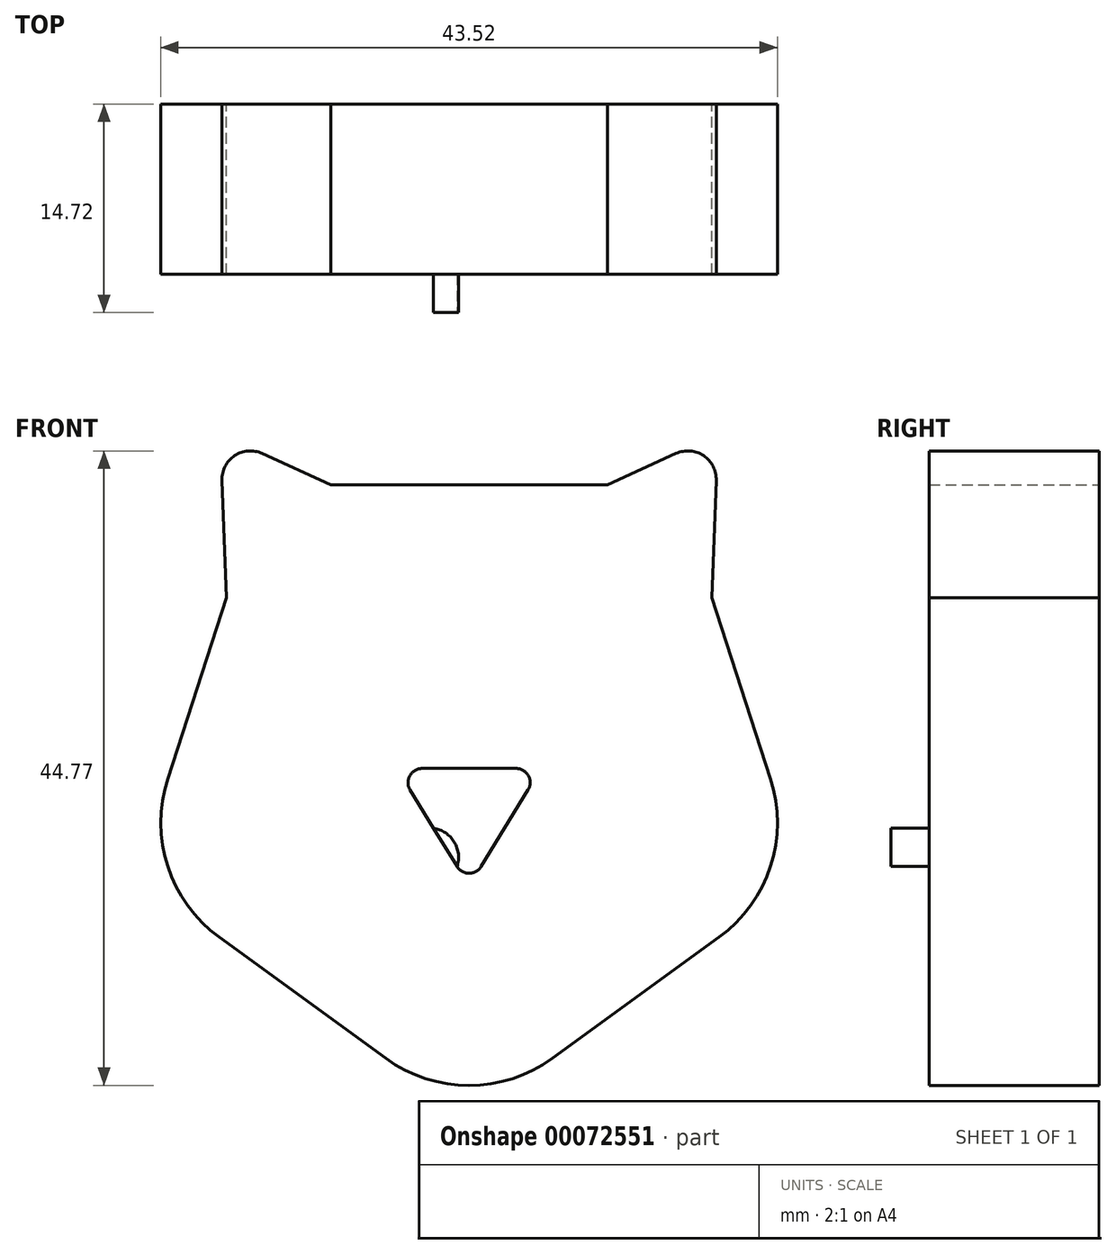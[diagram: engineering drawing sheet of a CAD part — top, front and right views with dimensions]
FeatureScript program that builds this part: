
annotation { "Feature Type Name" : "Feature", "Feature Type Description" : "" }
export const myFeature = defineFeature(function(context is Context, id is Id, definition is map)
    precondition{}
    {
        {
            var Q0;
            Q0=qCreatedBy(makeId("Front.planeOp"),FACE);
            var sketch = newSketch(context, id + "F0", { "sketchPlane" : qUnion([Q0])});
            skCircle(sketch, "E0.cCircle", {"center": v(0, 0) * mm, "radius": 20 * mm, "construction": true});
            skLineSegment(sketch, "E0.0", {"start": v(0, -24.72) * mm, "end": v(-23.51, -7.64) * mm});
            skLineSegment(sketch, "E0.1", {"start": v(-23.51, -7.64) * mm, "end": v(-14.53, 20) * mm});
            skLineSegment(sketch, "E0.2", {"start": v(-14.53, 20) * mm, "end": v(14.53, 20) * mm});
            skLineSegment(sketch, "E0.3", {"start": v(14.53, 20) * mm, "end": v(23.51, -7.64) * mm});
            skLineSegment(sketch, "E0.4", {"start": v(23.51, -7.64) * mm, "end": v(0, -24.72) * mm});
            skPoint(sketch, "E0.0.midPoint", {"position": v(-11.76, -16.18) * mm});
            skPoint(sketch, "E1.0.midPoint", {"position": v(19.33, 5.13) * mm});
            skSolve(sketch);
        }
        {
            var Q0;
            Q0=makeQuery(id+"F0.imprint","IMPRINT",FACE,{"disambiguationData":[TD([[makeQuery(id+"F0.imprint","IMPRINT",EDGE,{"derivedFrom":sQuery(id+"F0.wireOp",EDGE,"E0.0")}),-1.0]])]});
            extrude(context, id + "F1", {"entities" : qUnion([Q0]), "endBound" : BoundingType.SYMMETRIC, "depth" : 12 * mm});
        }
        {
            var Q0;
            Q0=qCreatedBy(makeId("Front.planeOp"),FACE);
            var sketch = newSketch(context, id + "F2", { "sketchPlane" : qUnion([Q0])});
            skLineSegment(sketch, "E2", {"start": v(-17.12, 12.04) * mm, "end": v(-17.56, 23.58) * mm});
            skLineSegment(sketch, "E3", {"start": v(-17.56, 23.58) * mm, "end": v(-9.75, 20) * mm});
            skLineSegment(sketch, "E4", {"start": v(-9.75, 20) * mm, "end": v(-17.12, 12.04) * mm});
            skLineSegment(sketch, "E5", {"start": v(0, 29) * mm, "end": v(0, 12.45) * mm});
            skLineSegment(sketch, "E6.MirrorCS", {"start": v(9.75, 20) * mm, "end": v(17.12, 12.04) * mm});
            skLineSegment(sketch, "E7.MirrorCS", {"start": v(17.56, 23.58) * mm, "end": v(9.75, 20) * mm});
            skLineSegment(sketch, "E8.MirrorCS", {"start": v(17.12, 12.04) * mm, "end": v(17.56, 23.58) * mm});
            skSolve(sketch);
        }
        {
            var Q0;
            Q0=makeQuery(id+"F2.imprint","IMPRINT",FACE,{"disambiguationData":[TD([[makeQuery(id+"F2.imprint","IMPRINT",EDGE,{"derivedFrom":sQuery(id+"F2.wireOp",EDGE,"E2")}),-1.0]])]});
            var Q1;
            Q1=makeQuery(id+"F2.imprint","IMPRINT",FACE,{"disambiguationData":[TD([[makeQuery(id+"F2.imprint","IMPRINT",EDGE,{"derivedFrom":sQuery(id+"F2.wireOp",EDGE,"E6.MirrorCS")}),1.0]])]});
            extrude(context, id + "F3", {"entities" : qUnion([Q0, Q1]), "operationType" : NewBodyOperationType.ADD, "endBound" : BoundingType.SYMMETRIC, "depth" : 12 * mm});
        }
        {
            var Q0;
            Q0=qCreatedBy(makeId("Front.planeOp"),FACE);
            var sketch = newSketch(context, id + "F4", { "sketchPlane" : qUnion([Q0])});
            skLineSegment(sketch, "E9", {"start": v(-21.03, 0) * mm, "end": v(0, 0) * mm, "construction": true});
            skLineSegment(sketch, "E10", {"start": v(-10.51, 0) * mm, "end": v(-10.51, 5.14) * mm, "construction": true});
            skCircle(sketch, "E11", {"center": v(-10.51, 5.14) * mm, "radius": 3.67 * mm});
            skLineSegment(sketch, "E12", {"start": v(0, 0) * mm, "end": v(0, 12.57) * mm, "construction": true});
            skCircle(sketch, "E13.MirrorC", {"center": v(10.51, 5.14) * mm, "radius": 3.67 * mm});
            skSolve(sketch);
        }
        {
            var Q0;
            Q0=makeQuery(id+"F3.opExtrude","SWEPT_EDGE",EDGE,{"disambiguationData":[OSD([sQuery(id+"F2.wireOp",EDGE,"E2"),sQuery(id+"F2.wireOp",EDGE,"E3")])]});
            var Q1;
            Q1=makeQuery(id+"F3.opExtrude","SWEPT_EDGE",EDGE,{"disambiguationData":[OSD([sQuery(id+"F2.wireOp",EDGE,"E7.MirrorCS"),sQuery(id+"F2.wireOp",EDGE,"E8.MirrorCS")])]});
            fillet(context, id + "F5", {"entities" : qUnion([Q0, Q1]), "radius" : 2 * mm, "tangentPropagation" : true, "allowEdgeOverflow" : false});
        }
        {
            var Q0;
            Q0=makeQuery(id+"F1.opExtrude","SWEPT_EDGE",EDGE,{"disambiguationData":[OSD([sQuery(id+"F0.wireOp",EDGE,"E0.0"),sQuery(id+"F0.wireOp",EDGE,"E0.1")])]});
            var Q1;
            Q1=makeQuery(id+"F1.opExtrude","SWEPT_EDGE",EDGE,{"disambiguationData":[OSD([sQuery(id+"F0.wireOp",EDGE,"E0.3"),sQuery(id+"F0.wireOp",EDGE,"E0.4")])]});
            var Q2;
            Q2=makeQuery(id+"F1.opExtrude","SWEPT_EDGE",EDGE,{"disambiguationData":[OSD([sQuery(id+"F0.wireOp",EDGE,"E0.0"),sQuery(id+"F0.wireOp",EDGE,"E0.4")])]});
            fillet(context, id + "F6", {"entities" : qUnion([Q0, Q1, Q2]), "radius" : 10 * mm, "tangentPropagation" : true, "allowEdgeOverflow" : false});
        }
        {
            var Q0;
            Q0=sQuery(id+"F4.wireOp",EDGE,"E11");
            var Q1;
            Q1=sQuery(id+"F4.wireOp",EDGE,"E13.MirrorC");
            extrude(context, id + "F7", {"bodyType" : ToolBodyType.SURFACE, "surfaceEntities" : qUnion([Q0, Q1]), "depth" : 7 * mm});
        }
        {
            var Q0;
            Q0=makeQuery(id+"F3.boolean.opBoolean","MERGE",FACE,{"derivedFrom":[makeQuery(id+"F1.opExtrude","CAP_FACE",FACE,{"disambiguationData":[OSD([sQuery(id+"F0.wireOp",EDGE,"E0.0"),sQuery(id+"F0.wireOp",EDGE,"E0.1"),sQuery(id+"F0.wireOp",EDGE,"E0.2"),sQuery(id+"F0.wireOp",EDGE,"E0.3"),sQuery(id+"F0.wireOp",EDGE,"E0.4")])],"isStart":false}),makeQuery(id+"F3.opExtrude","CAP_FACE",FACE,{"disambiguationData":[OSD([sQuery(id+"F2.wireOp",EDGE,"E2"),sQuery(id+"F2.wireOp",EDGE,"E3"),sQuery(id+"F2.wireOp",EDGE,"E4")])],"isStart":false}),makeQuery(id+"F3.opExtrude","CAP_FACE",FACE,{"disambiguationData":[OSD([sQuery(id+"F2.wireOp",EDGE,"E6.MirrorCS"),sQuery(id+"F2.wireOp",EDGE,"E7.MirrorCS"),sQuery(id+"F2.wireOp",EDGE,"E8.MirrorCS")])],"isStart":false})]});
            var sketch = newSketch(context, id + "F8", { "sketchPlane" : qUnion([Q0])});
            skLineSegment(sketch, "E14", {"start": v(-5.1, 0) * mm, "end": v(5.1, 0) * mm});
            skLineSegment(sketch, "E15", {"start": v(5.1, 0) * mm, "end": v(0, -8.32) * mm});
            skLineSegment(sketch, "E16", {"start": v(0, -8.32) * mm, "end": v(-5.1, 0) * mm});
            skSolve(sketch);
        }
        {
            var Q0;
            Q0=makeQuery(id+"F8.imprint","IMPRINT",FACE,{"disambiguationData":[TD([[makeQuery(id+"F8.imprint","IMPRINT",EDGE,{"derivedFrom":sQuery(id+"F8.wireOp",EDGE,"E14")}),-1.0]])]});
            extrude(context, id + "F9", {"entities" : qUnion([Q0]), "operationType" : NewBodyOperationType.ADD, "depth" : 2.72 * mm});
        }
        {
            var Q0;
            Q0=makeQuery(id+"F9.opExtrude","SWEPT_EDGE",EDGE,{"disambiguationData":[OSD([sQuery(id+"F8.wireOp",EDGE,"E15"),sQuery(id+"F8.wireOp",EDGE,"E16")])]});
            var Q1;
            Q1=makeQuery(id+"F9.opExtrude","SWEPT_EDGE",EDGE,{"disambiguationData":[OSD([sQuery(id+"F8.wireOp",EDGE,"E14"),sQuery(id+"F8.wireOp",EDGE,"E16")])]});
            var Q2;
            Q2=makeQuery(id+"F9.opExtrude","SWEPT_EDGE",EDGE,{"disambiguationData":[OSD([sQuery(id+"F8.wireOp",EDGE,"E14"),sQuery(id+"F8.wireOp",EDGE,"E15")])]});
            fillet(context, id + "F10", {"entities" : qUnion([Q0, Q1, Q2]), "radius" : 1 * mm, "tangentPropagation" : true, "allowEdgeOverflow" : false});
        }
        {
            var Q0;
            Q0=qCreatedBy(makeId("Front.planeOp"),FACE);
            cPlane(context, id + "F11", {"entities" : qUnion([Q0]), "cplaneType" : CPlaneType.OFFSET, "offset" : 8 * mm, "width" : 152.4 * mm, "height" : 152.4 * mm});
        }
        {
            var Q0;
            Q0=qCreatedBy(id+"F11.planeOp",FACE);
            var sketch = newSketch(context, id + "F12", { "sketchPlane" : qUnion([Q0])});
            skLineSegment(sketch, "E17", {"start": v(-10.51, 8.81) * mm, "end": v(-10.51, 1.48) * mm, "construction": true});
            skLineSegment(sketch, "E18", {"start": v(0, 8.43) * mm, "end": v(0, 3.77) * mm, "construction": true});
            skLineSegment(sketch, "E19.MirrorCS", {"start": v(10.51, 8.81) * mm, "end": v(10.51, 1.48) * mm, "construction": true});
            skPoint(sketch, "E20", {"position": v(-10.51, 5.14) * mm});
            skPoint(sketch, "E21", {"position": v(10.51, 5.14) * mm});
            skSolve(sketch);
        }
        {
            var Q0;
            Q0=sQuery(id+"F12.wireOp",VERTEX,"E20");
            var Q1;
            Q1=makeQuery(id+"F3.boolean.opBoolean","MERGE",FACE,{"derivedFrom":[makeQuery(id+"F1.opExtrude","CAP_FACE",FACE,{"disambiguationData":[OSD([sQuery(id+"F0.wireOp",EDGE,"E0.0"),sQuery(id+"F0.wireOp",EDGE,"E0.1"),sQuery(id+"F0.wireOp",EDGE,"E0.2"),sQuery(id+"F0.wireOp",EDGE,"E0.3"),sQuery(id+"F0.wireOp",EDGE,"E0.4")])],"isStart":false}),makeQuery(id+"F3.opExtrude","CAP_FACE",FACE,{"disambiguationData":[OSD([sQuery(id+"F2.wireOp",EDGE,"E2"),sQuery(id+"F2.wireOp",EDGE,"E3"),sQuery(id+"F2.wireOp",EDGE,"E4")])],"isStart":false}),makeQuery(id+"F3.opExtrude","CAP_FACE",FACE,{"disambiguationData":[OSD([sQuery(id+"F2.wireOp",EDGE,"E6.MirrorCS"),sQuery(id+"F2.wireOp",EDGE,"E7.MirrorCS"),sQuery(id+"F2.wireOp",EDGE,"E8.MirrorCS")])],"isStart":false})]});
            var Q2;
            Q2=sQuery(id+"F12.wireOp",VERTEX,"E21");
            var Q3;
            Q3=makeQuery(id+"F7.opExtrude","CAP_EDGE",EDGE,{"disambiguationData":[OSD([sQuery(id+"F4.wireOp",EDGE,"E13.MirrorC")])],"isStart":false});
            loft(context, id + "F13", {"bodyType" : ToolBodyType.SURFACE, "sheetProfilesArray" : [{ "sheetProfileEntities" : qUnion([Q0]) }, { "sheetProfileEntities" : qUnion([Q1]) }], "wireProfilesArray" : [{ "wireProfileEntities" : qUnion([Q2]) }, { "wireProfileEntities" : qUnion([Q3]) }]});
        }
        {
            var Q0;
            Q0=qCreatedBy(makeId("Front.planeOp"),FACE);
            cPlane(context, id + "F14", {"entities" : qUnion([Q0]), "cplaneType" : CPlaneType.OFFSET, "offset" : 8 * mm, "width" : 152.4 * mm, "height" : 152.4 * mm});
        }
        {
            var Q0;
            Q0=qCreatedBy(id+"F14.planeOp",FACE);
            var sketch = newSketch(context, id + "F15", { "sketchPlane" : qUnion([Q0])});
            skPoint(sketch, "E22", {"position": v(-10.51, 5.14) * mm});
            skLineSegment(sketch, "E23", {"start": v(-10.51, 8.81) * mm, "end": v(-10.51, 1.48) * mm, "construction": true});
            skSolve(sketch);
        }
        {
            var Q0;
            Q0=sQuery(id+"F15.wireOp",VERTEX,"E22");
            var Q1;
            Q1=makeQuery(id+"F7.opExtrude","CAP_EDGE",EDGE,{"disambiguationData":[OSD([sQuery(id+"F4.wireOp",EDGE,"E11")])],"isStart":false});
            loft(context, id + "F16", {"bodyType" : ToolBodyType.SURFACE, "wireProfilesArray" : [{ "wireProfileEntities" : qUnion([Q0]) }, { "wireProfileEntities" : qUnion([Q1]) }]});
        }
        {
            var Q0;
            Q0=makeQuery(id+"F9.opExtrude","CAP_FACE",FACE,{"disambiguationData":[OSD([sQuery(id+"F8.wireOp",EDGE,"E14"),sQuery(id+"F8.wireOp",EDGE,"E15"),sQuery(id+"F8.wireOp",EDGE,"E16")])],"isStart":false});
            var sketch = newSketch(context, id + "F17", { "sketchPlane" : qUnion([Q0])});
            skArc(sketch, "E24", {"start": v(2.5, -4.22) * mm, "mid": v(1.05, -5.19) * mm, "end": v(0.85, -6.92) * mm});
            skLineSegment(sketch, "E25", {"start": v(0, -2.33) * mm, "end": v(0, -5.64) * mm, "construction": true});
            skArc(sketch, "E26.MirrorCS", {"start": v(-2.5, -4.22) * mm, "mid": v(-1.05, -5.19) * mm, "end": v(-0.85, -6.92) * mm});
            skSolve(sketch);
        }
        {
            var Q0;
            {var subQ0=sQuery(id+"F17.wireOp",EDGE,"E24");Q0=makeQuery(id+"F17.imprint","IMPRINT",FACE,{"disambiguationData":[TD([[makeQuery(id+"F17.imprint","IMPRINT",EDGE,{"derivedFrom":subQ0}),1.0]])]});}
            var Q1;
            {var subQ0=sQuery(id+"F17.wireOp",EDGE,"E26.MirrorCS");Q1=makeQuery(id+"F17.imprint","IMPRINT",FACE,{"disambiguationData":[TD([[makeQuery(id+"F17.imprint","IMPRINT",EDGE,{"derivedFrom":subQ0}),-1.0]])]});}
            var Q2;
            Q2=makeQuery(id+"F6.opFillet","BLEND_FACE",FACE,{"disambiguationData":[OSD([sQuery(id+"F0.wireOp",EDGE,"E0.0"),sQuery(id+"F0.wireOp",EDGE,"E0.1")])]});
            extrude(context, id + "F18", {"entities" : qUnion([Q0, Q1]), "operationType" : NewBodyOperationType.REMOVE, "oppositeDirection" : true, "endBoundEntityFace" : qUnion([Q2]), "depth" : 2.7 * mm});
        }
        {
            var Q0;
            Q0=makeQuery(id+"F3.boolean.opBoolean","MERGE",FACE,{"derivedFrom":[makeQuery(id+"F1.opExtrude","CAP_FACE",FACE,{"disambiguationData":[OSD([sQuery(id+"F0.wireOp",EDGE,"E0.0"),sQuery(id+"F0.wireOp",EDGE,"E0.1"),sQuery(id+"F0.wireOp",EDGE,"E0.2"),sQuery(id+"F0.wireOp",EDGE,"E0.3"),sQuery(id+"F0.wireOp",EDGE,"E0.4")])],"isStart":true}),makeQuery(id+"F3.opExtrude","CAP_FACE",FACE,{"disambiguationData":[OSD([sQuery(id+"F2.wireOp",EDGE,"E2"),sQuery(id+"F2.wireOp",EDGE,"E3"),sQuery(id+"F2.wireOp",EDGE,"E4")])],"isStart":true}),makeQuery(id+"F3.opExtrude","CAP_FACE",FACE,{"disambiguationData":[OSD([sQuery(id+"F2.wireOp",EDGE,"E6.MirrorCS"),sQuery(id+"F2.wireOp",EDGE,"E7.MirrorCS"),sQuery(id+"F2.wireOp",EDGE,"E8.MirrorCS")])],"isStart":true})]});
            var sketch = newSketch(context, id + "F19", { "sketchPlane" : qUnion([Q0])});
            skEllipse(sketch, "E27", {"center": v(0, -39.15) * mm, "majorRadius": 32.58 * mm, "minorRadius": 17.87 * mm, "majorAxis": v(0, -1)});
            skSolve(sketch);
        }
        {
            var Q0;
            Q0=qCreatedBy(makeId("Front.planeOp"),FACE);
            cPlane(context, id + "F20", {"entities" : qUnion([Q0]), "cplaneType" : CPlaneType.OFFSET, "offset" : 70 * mm, "oppositeDirection" : true, "width" : 152.4 * mm, "height" : 152.4 * mm});
        }
        {
            var Q0;
            Q0=qCreatedBy(id+"F20.planeOp",FACE);
            var sketch = newSketch(context, id + "F21", { "sketchPlane" : qUnion([Q0])});
            skPoint(sketch, "E28", {"position": v(0, -39.15) * mm});
            skSolve(sketch);
        }
        {
            var Q0;
            Q0=qCreatedBy(makeId("Right.planeOp"),FACE);
            var sketch = newSketch(context, id + "F22", { "sketchPlane" : qUnion([Q0])});
            skLineSegment(sketch, "E29", {"start": v(6, -39.15) * mm, "end": v(70, -39.15) * mm, "construction": true});
            skFitSpline(sketch, "E30", {"points": [v(6, -8.86) * mm, v(38.4, -4) * mm, v(67.08, -14.86) * mm, v(112.75, -31.72) * mm], "startDerivative": vector(102.67, 28.88) * mm, "endDerivative": vector(126.13, -42.39) * mm});
            skSolve(sketch);
        }
        {
            var Q0;
            Q0 = qSketchRegion(id + "F22", true);
            var Q1;
            Q1=sQuery(id+"F22.wireOp",EDGE,"E30");
            var Q2;
            Q2=sQuery(id+"F22.wireOp",EDGE,"E29");
            revolve(context, id + "F23", {"bodyType" : ToolBodyType.SURFACE, "entities" : qUnion([Q0]), "surfaceEntities" : qUnion([Q1]), "axis" : qUnion([Q2]), "revolveType" : RevolveType.TWO_DIRECTIONS, "angle" : 120 * degree, "angleBack" : 240 * degree});
        }
    });
